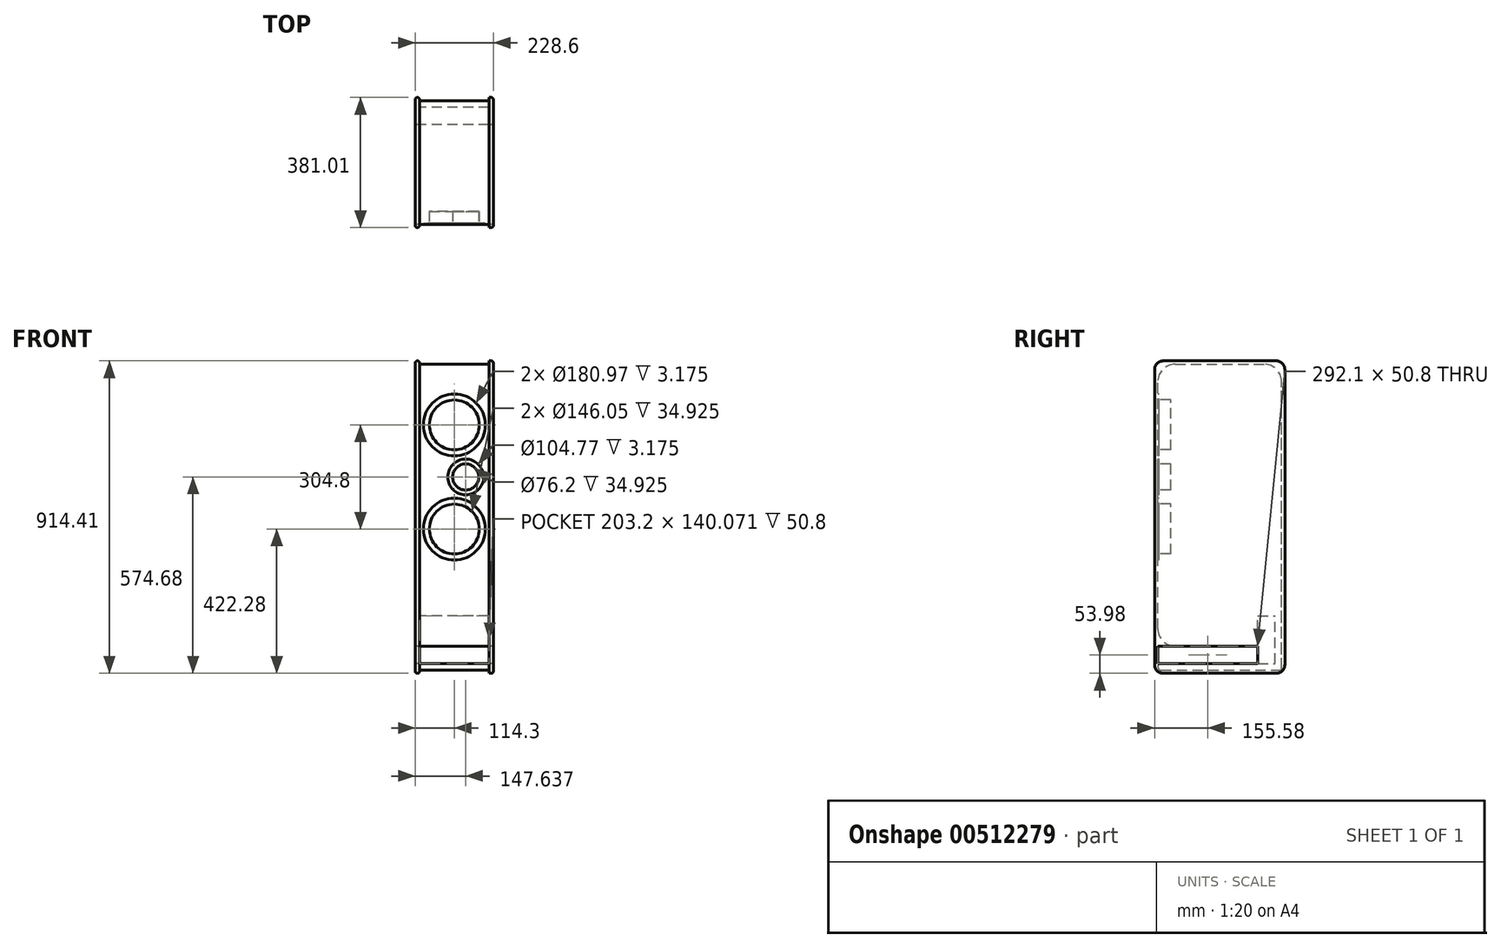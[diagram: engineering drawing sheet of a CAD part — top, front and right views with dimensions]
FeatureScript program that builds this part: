
annotation { "Feature Type Name" : "Feature", "Feature Type Description" : "" }
export const myFeature = defineFeature(function(context is Context, id is Id, definition is map)
    precondition{}
    {
        {
            var Q0;
            Q0=qCreatedBy(makeId("Right.planeOp"),FACE);
            var sketch = newSketch(context, id + "F0", { "sketchPlane" : qUnion([Q0])});
            skLineSegment(sketch, "E0.bottom", {"start": v(0, 0) * mm, "end": v(361.95, 0) * mm});
            skLineSegment(sketch, "E0.top", {"start": v(50.8, 895.35) * mm, "end": v(311.15, 895.35) * mm});
            skLineSegment(sketch, "E0.left", {"start": v(0, 0) * mm, "end": v(0, 844.55) * mm});
            skLineSegment(sketch, "E0.right", {"start": v(361.95, 0) * mm, "end": v(361.95, 844.55) * mm});
            skPoint(sketch, "E1.visualSharp", {"position": v(0, 895.35) * mm});
            skArc(sketch, "E1.filletArc", {"start": v(50.8, 895.35) * mm, "mid": v(14.88, 880.47) * mm, "end": v(0, 844.55) * mm});
            skLineSegment(sketch, "E2.bottom", {"start": v(0, 19.05) * mm, "end": v(292.1, 19.05) * mm});
            skLineSegment(sketch, "E2.top", {"start": v(0, 69.85) * mm, "end": v(292.1, 69.85) * mm});
            skLineSegment(sketch, "E2.left", {"start": v(0, 19.05) * mm, "end": v(0, 69.85) * mm});
            skLineSegment(sketch, "E2.right", {"start": v(292.1, 19.05) * mm, "end": v(292.1, 69.85) * mm});
            skLineSegment(sketch, "E3.bottom", {"start": v(292.1, 19.05) * mm, "end": v(342.9, 19.05) * mm});
            skLineSegment(sketch, "E3.top", {"start": v(292.1, 159.12) * mm, "end": v(342.9, 159.12) * mm});
            skLineSegment(sketch, "E3.left", {"start": v(292.1, 19.05) * mm, "end": v(292.1, 159.12) * mm});
            skLineSegment(sketch, "E3.right", {"start": v(342.9, 19.05) * mm, "end": v(342.9, 159.12) * mm});
            skArc(sketch, "E4", {"start": v(0, 120.65) * mm, "mid": v(14.88, 84.73) * mm, "end": v(50.8, 69.85) * mm});
            skLineSegment(sketch, "E5.bottom", {"start": v(15.87, 904.88) * mm, "end": v(346.07, 904.88) * mm});
            skLineSegment(sketch, "E5.top", {"start": v(15.87, -9.53) * mm, "end": v(346.08, -9.53) * mm});
            skLineSegment(sketch, "E5.left", {"start": v(-9.53, 879.48) * mm, "end": v(-9.52, 15.87) * mm});
            skLineSegment(sketch, "E5.right", {"start": v(371.47, 879.48) * mm, "end": v(371.48, 15.88) * mm});
            skPoint(sketch, "E6.visualSharp", {"position": v(-9.53, 904.88) * mm});
            skArc(sketch, "E6.filletArc", {"start": v(15.87, 904.88) * mm, "mid": v(-2.09, 897.44) * mm, "end": v(-9.53, 879.48) * mm});
            skPoint(sketch, "E7.visualSharp", {"position": v(361.95, 895.35) * mm});
            skArc(sketch, "E7.filletArc", {"start": v(361.95, 844.55) * mm, "mid": v(347.07, 880.47) * mm, "end": v(311.15, 895.35) * mm});
            skPoint(sketch, "E8.visualSharp", {"position": v(371.47, 904.88) * mm});
            skArc(sketch, "E8.filletArc", {"start": v(371.47, 879.48) * mm, "mid": v(364.04, 897.44) * mm, "end": v(346.07, 904.88) * mm});
            skPoint(sketch, "E9.visualSharp", {"position": v(-9.52, -9.53) * mm});
            skArc(sketch, "E9.filletArc", {"start": v(-9.53, 15.87) * mm, "mid": v(-2.09, -2.09) * mm, "end": v(15.87, -9.53) * mm});
            skPoint(sketch, "E10.visualSharp", {"position": v(371.48, -9.53) * mm});
            skArc(sketch, "E10.filletArc", {"start": v(346.08, -9.52) * mm, "mid": v(364.04, -2.09) * mm, "end": v(371.48, 15.88) * mm});
            skArc(sketch, "E11", {"start": v(9.52, 19.05) * mm, "mid": v(0, 9.52) * mm, "end": v(9.52, 0) * mm});
            skSolve(sketch);
        }
        {
            var Q0;
            Q0=makeQuery(id+"F0.imprint","IMPRINT",FACE,{"disambiguationData":[TD([[makeQuery(id+"F0.imprint","IMPRINT",EDGE,{"derivedFrom":sQuery(id+"F0.wireOp",EDGE,"E0.top")}),1.0]])]});
            var Q1;
            Q1=makeQuery(id+"F0.imprint","IMPRINT",FACE,{"disambiguationData":[TD([[makeQuery(id+"F0.imprint","IMPRINT",EDGE,{"derivedFrom":sQuery(id+"F0.wireOp",EDGE,"E0.top")}),-1.0]])]});
            var Q2;
            {var subQ3=sQuery(id+"F0.wireOp",EDGE,"E3.bottom");Q2=makeQuery(id+"F0.imprint","IMPRINT",FACE,{"disambiguationData":[TD([[makeQuery(id+"F0.imprint","IMPRINT",EDGE,{"derivedFrom":subQ3}),1.0]])]});}
            var Q3;
            {var subQ4=sQuery(id+"F0.wireOp",EDGE,"E2.left");Q3=makeQuery(id+"F0.imprint","IMPRINT",FACE,{"disambiguationData":[TD([[makeQuery(id+"F0.imprint","IMPRINT",EDGE,{"derivedFrom":subQ4}),-1.0]])]});}
            var Q4;
            {var subQ3=sQuery(id+"F0.wireOp",EDGE,"E4");Q4=makeQuery(id+"F0.imprint","IMPRINT",FACE,{"disambiguationData":[TD([[makeQuery(id+"F0.imprint","IMPRINT",EDGE,{"derivedFrom":subQ3}),-1.0]])]});}
            var Q5;
            {var subQ0=sQuery(id+"F0.wireOp",EDGE,"E0.left");var subQ1=sQuery(id+"F0.wireOp",EDGE,"E0.bottom");var subQ2=makeQuery(id+"F0.imprint","INTERSECT",VERTEX,{"derivedFrom":[subQ1,subQ0]});Q5=makeQuery(id+"F0.imprint","IMPRINT",FACE,{"disambiguationData":[TD([[makeQuery(id+"F0.imprint","IMPRINT",EDGE,{"disambiguationData":[TD([[subQ2,-1.0]])],"derivedFrom":subQ1}),1.0]])]});}
            var Q6;
            {var subQ0=sQuery(id+"F0.wireOp",EDGE,"E2.bottom");var subQ3=sQuery(id+"F0.wireOp",EDGE,"E11");var subQ5=makeQuery(id+"F0.imprint","INTERSECT",VERTEX,{"derivedFrom":[subQ0,subQ3]});Q6=makeQuery(id+"F0.imprint","IMPRINT",FACE,{"disambiguationData":[TD([[makeQuery(id+"F0.imprint","IMPRINT",EDGE,{"disambiguationData":[TD([[subQ5,-1.0]])],"derivedFrom":subQ3}),-1.0]])]});}
            extrude(context, id + "F1", {"entities" : qUnion([Q0, Q1, Q2, Q3, Q4, Q5, Q6]), "endBound" : BoundingType.SYMMETRIC, "depth" : 228.6 * mm});
        }
        {
            var Q0;
            Q0=makeQuery(id+"F0.imprint","IMPRINT",FACE,{"disambiguationData":[TD([[makeQuery(id+"F0.imprint","IMPRINT",EDGE,{"derivedFrom":sQuery(id+"F0.wireOp",EDGE,"E0.top")}),1.0]])]});
            var Q1;
            {var subQ3=sQuery(id+"F0.wireOp",EDGE,"E4");Q1=makeQuery(id+"F0.imprint","IMPRINT",FACE,{"disambiguationData":[TD([[makeQuery(id+"F0.imprint","IMPRINT",EDGE,{"derivedFrom":subQ3}),-1.0]])]});}
            var Q2;
            {var subQ3=sQuery(id+"F0.wireOp",EDGE,"E3.bottom");Q2=makeQuery(id+"F0.imprint","IMPRINT",FACE,{"disambiguationData":[TD([[makeQuery(id+"F0.imprint","IMPRINT",EDGE,{"derivedFrom":subQ3}),1.0]])]});}
            var Q3;
            {var subQ4=sQuery(id+"F0.wireOp",EDGE,"E2.left");Q3=makeQuery(id+"F0.imprint","IMPRINT",FACE,{"disambiguationData":[TD([[makeQuery(id+"F0.imprint","IMPRINT",EDGE,{"derivedFrom":subQ4}),-1.0]])]});}
            var Q4;
            {var subQ0=sQuery(id+"F0.wireOp",EDGE,"E0.left");var subQ1=sQuery(id+"F0.wireOp",EDGE,"E0.bottom");var subQ2=makeQuery(id+"F0.imprint","INTERSECT",VERTEX,{"derivedFrom":[subQ1,subQ0]});Q4=makeQuery(id+"F0.imprint","IMPRINT",FACE,{"disambiguationData":[TD([[makeQuery(id+"F0.imprint","IMPRINT",EDGE,{"disambiguationData":[TD([[subQ2,-1.0]])],"derivedFrom":subQ1}),1.0]])]});}
            var Q5;
            {var subQ0=sQuery(id+"F0.wireOp",EDGE,"E2.bottom");var subQ3=sQuery(id+"F0.wireOp",EDGE,"E11");var subQ5=makeQuery(id+"F0.imprint","INTERSECT",VERTEX,{"derivedFrom":[subQ0,subQ3]});Q5=makeQuery(id+"F0.imprint","IMPRINT",FACE,{"disambiguationData":[TD([[makeQuery(id+"F0.imprint","IMPRINT",EDGE,{"disambiguationData":[TD([[subQ5,-1.0]])],"derivedFrom":subQ3}),-1.0]])]});}
            extrude(context, id + "F2", {"entities" : qUnion([Q0, Q1, Q2, Q3, Q4, Q5]), "operationType" : NewBodyOperationType.REMOVE, "endBound" : BoundingType.SYMMETRIC, "depth" : 203.2 * mm});
        }
        {
            var Q0;
            Q0=makeQuery(id+"F1.opExtrude","CAP_EDGE",EDGE,{"disambiguationData":[OSD([sQuery(id+"F0.wireOp",EDGE,"E5.left")])],"isStart":true});
            var Q1;
            Q1=makeQuery(id+"F2.boolean.opBoolean","COPY",EDGE,{"derivedFrom":makeQuery(id+"F2.opExtrude","CAP_EDGE",EDGE,{"disambiguationData":[OSD([sQuery(id+"F0.wireOp",EDGE,"E5.left")])],"isStart":true})});
            var Q2;
            Q2=makeQuery(id+"F2.boolean.opBoolean","COPY",EDGE,{"derivedFrom":makeQuery(id+"F2.opExtrude","CAP_EDGE",EDGE,{"disambiguationData":[OSD([sQuery(id+"F0.wireOp",EDGE,"E5.left")])],"isStart":false})});
            var Q3;
            Q3=makeQuery(id+"F1.opExtrude","CAP_EDGE",EDGE,{"disambiguationData":[OSD([sQuery(id+"F0.wireOp",EDGE,"E5.left")])],"isStart":false});
            fillet(context, id + "F3", {"entities" : qUnion([Q0, Q1, Q2, Q3]), "radius" : 6.35 * mm, "tangentPropagation" : true, "allowEdgeOverflow" : false});
        }
        {
            var Q0;
            Q0=makeQuery(id+"F2.boolean.opBoolean","COPY",FACE,{"derivedFrom":makeQuery(id+"F2.opExtrude","SWEPT_FACE",FACE,{"disambiguationData":[OSD([sQuery(id+"F0.wireOp",EDGE,"E0.left")])]})});
            var sketch = newSketch(context, id + "F4", { "sketchPlane" : qUnion([Q0])});
            skCircle(sketch, "E12", {"center": v(0, 717.55) * mm, "radius": 90.49 * mm});
            skCircle(sketch, "E13", {"center": v(0, 717.55) * mm, "radius": 73.03 * mm});
            skLineSegment(sketch, "E14", {"start": v(-190.1, 565.15) * mm, "end": v(234.48, 565.15) * mm});
            skCircle(sketch, "E15", {"center": v(33.34, 565.15) * mm, "radius": 52.39 * mm});
            skCircle(sketch, "E16", {"center": v(0, 412.75) * mm, "radius": 73.03 * mm});
            skCircle(sketch, "E17", {"center": v(0, 412.75) * mm, "radius": 90.49 * mm});
            skCircle(sketch, "E18", {"center": v(33.34, 565.15) * mm, "radius": 38.1 * mm});
            skSolve(sketch);
        }
        {
            var Q0;
            {var subQ0=sQuery(id+"F4.wireOp",EDGE,"E15");var subQ1=sQuery(id+"F4.wireOp",EDGE,"E14");var subQ2=makeQuery(id+"F4.imprint","INTERSECT",VERTEX,{"disambiguationData":[OD(0.0)],"derivedFrom":[subQ1,subQ0]});Q0=makeQuery(id+"F4.imprint","IMPRINT",FACE,{"disambiguationData":[TD([[makeQuery(id+"F4.imprint","IMPRINT",EDGE,{"disambiguationData":[TD([[subQ2,-1.0]])],"derivedFrom":subQ1}),-1.0]])]});}
            var Q1;
            {var subQ0=sQuery(id+"F4.wireOp",EDGE,"E15");var subQ1=sQuery(id+"F4.wireOp",EDGE,"E14");var subQ2=makeQuery(id+"F4.imprint","INTERSECT",VERTEX,{"disambiguationData":[OD(0.0)],"derivedFrom":[subQ1,subQ0]});Q1=makeQuery(id+"F4.imprint","IMPRINT",FACE,{"disambiguationData":[TD([[makeQuery(id+"F4.imprint","IMPRINT",EDGE,{"disambiguationData":[TD([[subQ2,-1.0]])],"derivedFrom":subQ1}),1.0]])]});}
            var Q2;
            Q2=makeQuery(id+"F4.imprint","IMPRINT",FACE,{"disambiguationData":[TD([[makeQuery(id+"F4.imprint","IMPRINT",EDGE,{"derivedFrom":sQuery(id+"F4.wireOp",EDGE,"E12")}),1.0]])]});
            var Q3;
            Q3=makeQuery(id+"F4.imprint","IMPRINT",FACE,{"disambiguationData":[TD([[makeQuery(id+"F4.imprint","IMPRINT",EDGE,{"derivedFrom":sQuery(id+"F4.wireOp",EDGE,"E16")}),-1.0]])]});
            extrude(context, id + "F5", {"entities" : qUnion([Q0, Q1, Q2, Q3]), "operationType" : NewBodyOperationType.REMOVE, "oppositeDirection" : true, "depth" : 3.17 * mm});
        }
        {
            var Q0;
            Q0=makeQuery(id+"F5.boolean.opBoolean","SPLIT",FACE,{"disambiguationData":[TD([makeQuery(id+"F5.opExtrude","SWEPT_FACE",FACE,{"disambiguationData":[OSD([sQuery(id+"F4.wireOp",EDGE,"E13")])]})])],"derivedFrom":makeQuery(id+"F2.boolean.opBoolean","COPY",FACE,{"derivedFrom":makeQuery(id+"F2.opExtrude","SWEPT_FACE",FACE,{"disambiguationData":[OSD([sQuery(id+"F0.wireOp",EDGE,"E0.left")])]})})});
            var Q1;
            Q1=makeQuery(id+"F5.boolean.opBoolean","SPLIT",FACE,{"disambiguationData":[TD([makeQuery(id+"F5.opExtrude","SWEPT_FACE",FACE,{"disambiguationData":[OSD([sQuery(id+"F4.wireOp",EDGE,"E18")])]})])],"derivedFrom":makeQuery(id+"F2.boolean.opBoolean","COPY",FACE,{"derivedFrom":makeQuery(id+"F2.opExtrude","SWEPT_FACE",FACE,{"disambiguationData":[OSD([sQuery(id+"F0.wireOp",EDGE,"E0.left")])]})})});
            var Q2;
            Q2=makeQuery(id+"F5.boolean.opBoolean","SPLIT",FACE,{"disambiguationData":[TD([makeQuery(id+"F5.opExtrude","SWEPT_FACE",FACE,{"disambiguationData":[OSD([sQuery(id+"F4.wireOp",EDGE,"E16")])]})])],"derivedFrom":makeQuery(id+"F2.boolean.opBoolean","COPY",FACE,{"derivedFrom":makeQuery(id+"F2.opExtrude","SWEPT_FACE",FACE,{"disambiguationData":[OSD([sQuery(id+"F0.wireOp",EDGE,"E0.left")])]})})});
            extrude(context, id + "F6", {"entities" : qUnion([Q0, Q1, Q2]), "operationType" : NewBodyOperationType.REMOVE, "oppositeDirection" : true, "depth" : 38.1 * mm});
        }
    });
